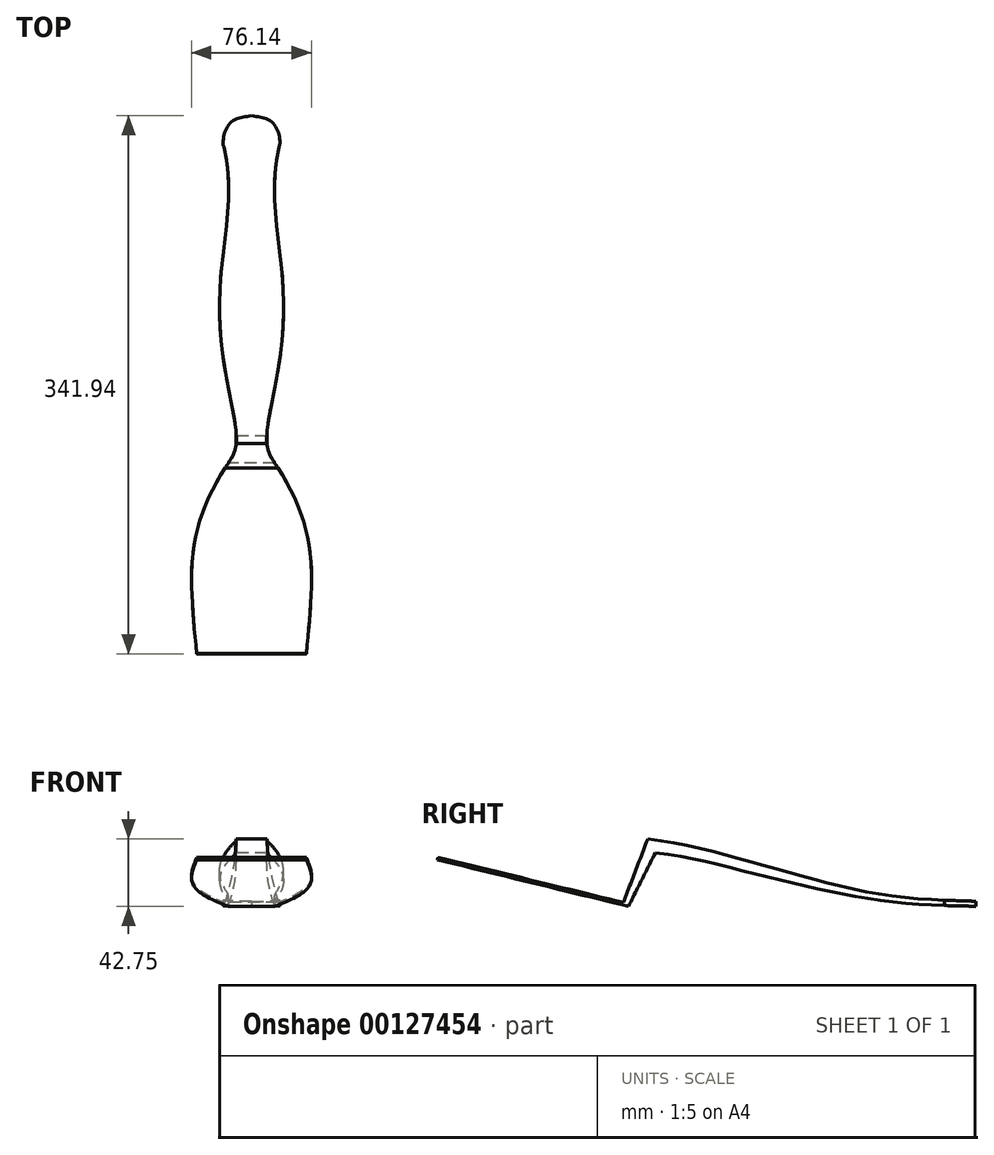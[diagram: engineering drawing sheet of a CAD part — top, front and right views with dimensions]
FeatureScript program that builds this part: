
annotation { "Feature Type Name" : "Feature", "Feature Type Description" : "" }
export const myFeature = defineFeature(function(context is Context, id is Id, definition is map)
    precondition{}
    {
        {
            var Q0;
            Q0=qCreatedBy(makeId("Right.planeOp"),FACE);
            var sketch = newSketch(context, id + "F0", { "sketchPlane" : qUnion([Q0])});
            skLineSegment(sketch, "E0", {"start": v(0, 0) * mm, "end": v(17.03, 33.87) * mm});
            skLineSegment(sketch, "E1", {"start": v(0, 0) * mm, "end": v(-121.3, 29.51) * mm});
            skLineSegment(sketch, "E2", {"start": v(-121.3, 29.51) * mm, "end": v(-120.93, 31.06) * mm});
            skLineSegment(sketch, "E3", {"start": v(-120.93, 31.06) * mm, "end": v(-3.19, 2.4) * mm});
            skFitSpline(sketch, "E4", {"points": [v(17.03, 33.87) * mm, v(45.8, 29.1) * mm, v(151.43, 5) * mm, v(220.63, 0) * mm], "startDerivative": vector(112.5, -8.17) * mm, "endDerivative": vector(190.06, -4.12) * mm});
            skLineSegment(sketch, "E5", {"start": v(220.63, 0) * mm, "end": v(220.63, 3.17) * mm});
            skFitSpline(sketch, "E6", {"points": [v(220.63, 3.17) * mm, v(198.43, 3.98) * mm, v(148.28, 9.72) * mm, v(48.58, 36.14) * mm, v(12.24, 42.75) * mm], "startDerivative": vector(-123.5, 3.56) * mm, "endDerivative": vector(-141.5, 19.2) * mm});
            skLineSegment(sketch, "E7", {"start": v(12.24, 42.75) * mm, "end": v(-3.19, 2.4) * mm});
            skSolve(sketch);
        }
        {
            var Q0;
            Q0 = qSketchRegion(id + "F0", true);
            extrude(context, id + "F1", {"entities" : qUnion([Q0]), "endBound" : BoundingType.SYMMETRIC, "depth" : 76.2 * mm});
        }
        {
            var Q0;
            Q0=qCreatedBy(makeId("Top.planeOp"),FACE);
            var sketch = newSketch(context, id + "F2", { "sketchPlane" : qUnion([Q0])});
            skFitSpline(sketch, "E8", {"points": [v(0, 220.66) * mm, v(-14.05, 215.47) * mm, v(-17.55, 200.54) * mm], "startDerivative": vector(-30.05, -6.52) * mm, "endDerivative": vector(8.14, -16.83) * mm});
            skFitSpline(sketch, "E9", {"points": [v(-17.55, 200.54) * mm, v(-18.75, 126.9) * mm, v(-17.55, 63.43) * mm, v(-9.8, 12.17) * mm, v(-17.55, -4.34) * mm, v(-35.75, -47.74) * mm, v(-34.8, -121.3) * mm], "startDerivative": vector(95.17, -401.12) * mm, "endDerivative": vector(38, -393.9) * mm});
            skLineSegment(sketch, "E10", {"start": v(-34.8, -121.3) * mm, "end": v(0, -121.3) * mm});
            skLineSegment(sketch, "E11", {"start": v(0, -121.3) * mm, "end": v(0, 220.66) * mm, "construction": true});
            skFitSpline(sketch, "E12.MirrorCS", {"points": [v(0, 220.66) * mm, v(14.05, 215.47) * mm, v(17.55, 200.54) * mm], "startDerivative": vector(30.05, -6.52) * mm, "endDerivative": vector(-8.14, -16.83) * mm});
            skLineSegment(sketch, "E13.MirrorCS", {"start": v(34.8, -121.3) * mm, "end": v(0, -121.3) * mm});
            skFitSpline(sketch, "E14.MirrorCS", {"points": [v(17.55, 200.54) * mm, v(18.75, 126.9) * mm, v(17.55, 63.43) * mm, v(9.8, 12.17) * mm, v(17.55, -4.34) * mm, v(35.75, -47.74) * mm, v(34.8, -121.3) * mm], "startDerivative": vector(-95.17, -401.12) * mm, "endDerivative": vector(-38, -393.9) * mm});
            skLineSegment(sketch, "E15.bottom", {"start": v(-93.57, 250.6) * mm, "end": v(84.54, 250.6) * mm});
            skLineSegment(sketch, "E15.top", {"start": v(-93.57, -163.5) * mm, "end": v(84.54, -163.5) * mm});
            skLineSegment(sketch, "E15.left", {"start": v(-93.57, 250.6) * mm, "end": v(-93.57, -163.5) * mm});
            skLineSegment(sketch, "E15.right", {"start": v(84.54, 250.6) * mm, "end": v(84.54, -163.5) * mm});
            skSolve(sketch);
        }
        {
            var Q0;
            Q0 = qSketchRegion(id + "F2", true);
            extrude(context, id + "F3", {"entities" : qUnion([Q0]), "operationType" : NewBodyOperationType.REMOVE, "depth" : 127 * mm});
        }
    });
